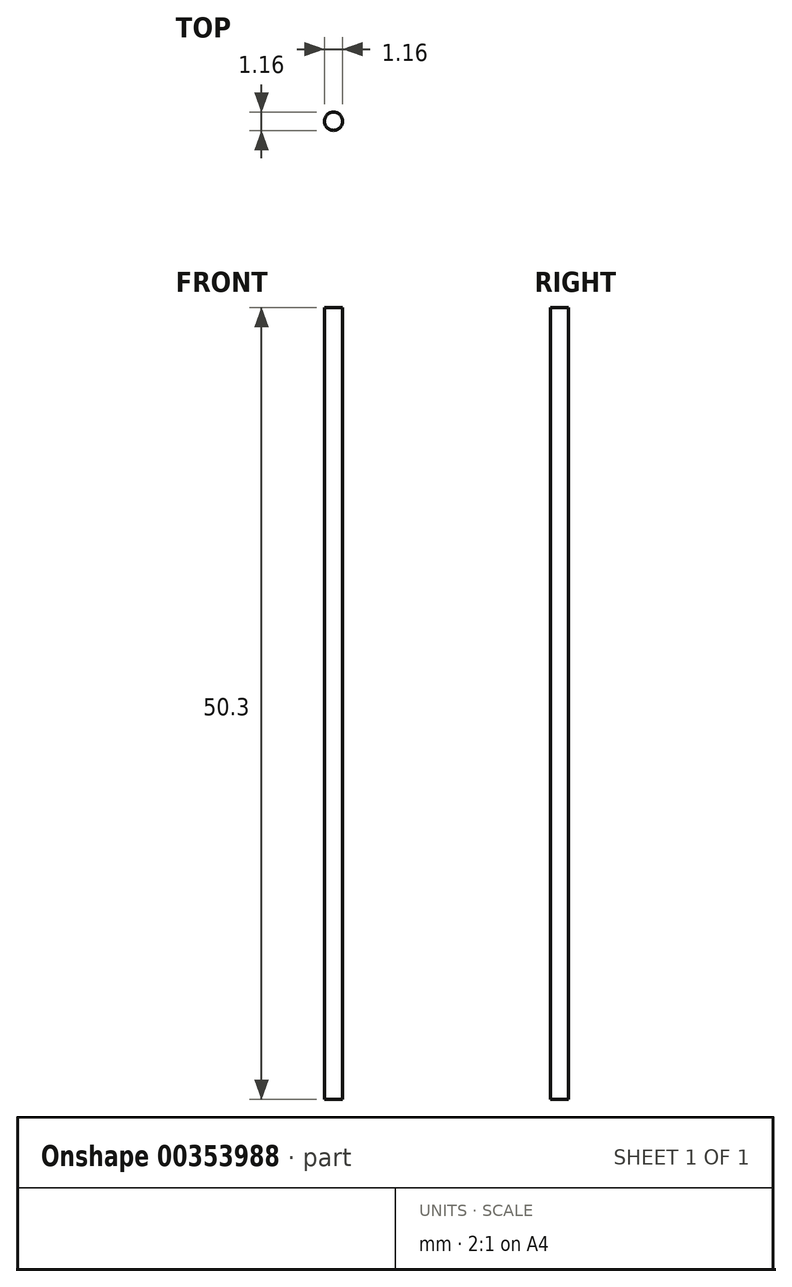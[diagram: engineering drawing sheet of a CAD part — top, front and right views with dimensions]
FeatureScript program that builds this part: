
annotation { "Feature Type Name" : "Feature", "Feature Type Description" : "" }
export const myFeature = defineFeature(function(context is Context, id is Id, definition is map)
    precondition{}
    {
        {
            var Q0;
            Q0=qCreatedBy(makeId("Top.planeOp"),FACE);
            var sketch = newSketch(context, id + "F0", { "sketchPlane" : qUnion([Q0])});
            skCircle(sketch, "E0", {"center": v(0, 0) * mm, "radius": 0.58 * mm});
            skSolve(sketch);
        }
        {
            var Q0;
            Q0=makeQuery(id+"F0.imprint","IMPRINT",FACE,{"disambiguationData":[TD([[makeQuery(id+"F0.imprint","IMPRINT",EDGE,{"derivedFrom":sQuery(id+"F0.wireOp",EDGE,"E0")}),1.0]])]});
            extrude(context, id + "F1", {"entities" : qUnion([Q0]), "endBound" : BoundingType.SYMMETRIC, "depth" : 50.3 * mm});
        }
    });
